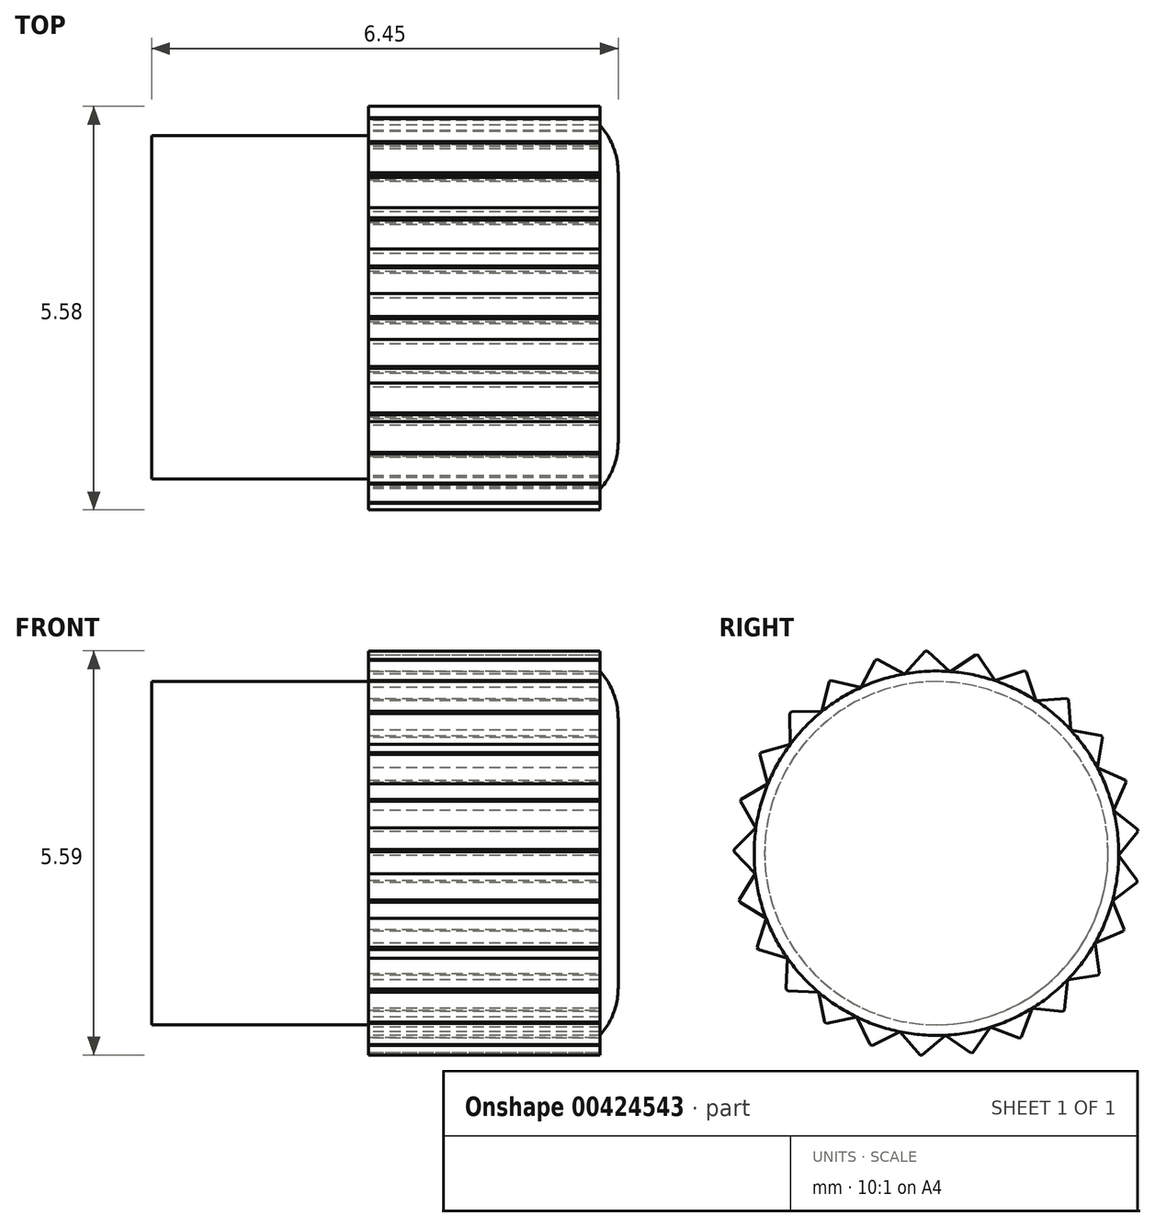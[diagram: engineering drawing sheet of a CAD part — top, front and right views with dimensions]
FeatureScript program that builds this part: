
annotation { "Feature Type Name" : "Feature", "Feature Type Description" : "" }
export const myFeature = defineFeature(function(context is Context, id is Id, definition is map)
    precondition{}
    {
        {
            var Q0;
            Q0=qCreatedBy(makeId("Right.planeOp"),FACE);
            var sketch = newSketch(context, id + "F0", { "sketchPlane" : qUnion([Q0])});
            skCircle(sketch, "E0.cCircle", {"center": v(0, 0) * mm, "radius": 2.5 * mm, "construction": true});
            skLineSegment(sketch, "E0.0", {"start": v(2.2, -1.24) * mm, "end": v(1.81, -1.75) * mm});
            skLineSegment(sketch, "E0.1", {"start": v(1.81, -1.75) * mm, "end": v(1.32, -2.14) * mm});
            skLineSegment(sketch, "E0.2", {"start": v(1.32, -2.14) * mm, "end": v(0.75, -2.4) * mm});
            skLineSegment(sketch, "E0.3", {"start": v(0.75, -2.4) * mm, "end": v(0.13, -2.52) * mm});
            skLineSegment(sketch, "E0.4", {"start": v(0.13, -2.52) * mm, "end": v(-0.5, -2.47) * mm});
            skLineSegment(sketch, "E0.5", {"start": v(-0.5, -2.47) * mm, "end": v(-1.1, -2.27) * mm});
            skLineSegment(sketch, "E0.6", {"start": v(-1.1, -2.27) * mm, "end": v(-1.63, -1.92) * mm});
            skLineSegment(sketch, "E0.7", {"start": v(-1.63, -1.92) * mm, "end": v(-2.06, -1.45) * mm});
            skLineSegment(sketch, "E0.8", {"start": v(-2.06, -1.45) * mm, "end": v(-2.35, -0.9) * mm});
            skLineSegment(sketch, "E0.9", {"start": v(-2.35, -0.9) * mm, "end": v(-2.5, -0.28) * mm});
            skLineSegment(sketch, "E0.10", {"start": v(-2.5, -0.28) * mm, "end": v(-2.5, 0.35) * mm});
            skLineSegment(sketch, "E0.11", {"start": v(-2.5, 0.35) * mm, "end": v(-2.33, 0.96) * mm});
            skLineSegment(sketch, "E0.12", {"start": v(-2.33, 0.96) * mm, "end": v(-2.02, 1.5) * mm});
            skLineSegment(sketch, "E0.13", {"start": v(-2.02, 1.5) * mm, "end": v(-1.58, 1.96) * mm});
            skLineSegment(sketch, "E0.14", {"start": v(-1.58, 1.96) * mm, "end": v(-1.04, 2.3) * mm});
            skLineSegment(sketch, "E0.15", {"start": v(-1.04, 2.3) * mm, "end": v(-0.44, 2.48) * mm});
            skLineSegment(sketch, "E0.16", {"start": v(-0.44, 2.48) * mm, "end": v(0.2, 2.51) * mm});
            skLineSegment(sketch, "E0.17", {"start": v(0.2, 2.51) * mm, "end": v(0.8, 2.39) * mm});
            skLineSegment(sketch, "E0.18", {"start": v(0.8, 2.39) * mm, "end": v(1.38, 2.1) * mm});
            skLineSegment(sketch, "E0.19", {"start": v(1.38, 2.1) * mm, "end": v(1.86, 1.7) * mm});
            skLineSegment(sketch, "E0.20", {"start": v(1.86, 1.7) * mm, "end": v(2.22, 1.19) * mm});
            skLineSegment(sketch, "E0.21", {"start": v(2.22, 1.19) * mm, "end": v(2.45, 0.6) * mm});
            skLineSegment(sketch, "E0.22", {"start": v(2.45, 0.6) * mm, "end": v(2.52, -0.03) * mm});
            skLineSegment(sketch, "E0.23", {"start": v(2.52, -0.03) * mm, "end": v(2.43, -0.66) * mm});
            skLineSegment(sketch, "E0.24", {"start": v(2.43, -0.66) * mm, "end": v(2.2, -1.24) * mm});
            skPoint(sketch, "E0.0.midPoint", {"position": v(2, -1.5) * mm});
            skSolve(sketch);
        }
        {
            var Q0;
            Q0=makeQuery(id+"F0.imprint","IMPRINT",FACE,{"disambiguationData":[TD([[makeQuery(id+"F0.imprint","IMPRINT",EDGE,{"derivedFrom":sQuery(id+"F0.wireOp",EDGE,"E0.0")}),-1.0]])]});
            extrude(context, id + "F1", {"entities" : qUnion([Q0]), "depth" : 3.2 * mm});
        }
        {
            var Q0;
            Q0=makeQuery(id+"F1.opExtrude","SWEPT_FACE",FACE,{"disambiguationData":[OSD([sQuery(id+"F0.wireOp",EDGE,"E0.14")])]});
            extrude(context, id + "F2", {"entities" : qUnion([Q0]), "operationType" : NewBodyOperationType.ADD, "depth" : .3 * mm});
        }
        {
            var Q0;
            Q0=makeQuery(id+"F2.opExtrude","CAP_EDGE",EDGE,{"disambiguationData":[OSD([sQuery(id+"F0.wireOp",EDGE,"E0.13"),sQuery(id+"F0.wireOp",EDGE,"E0.14")])],"isStart":false});
            var Q1;
            Q1=makeQuery(id+"F2.opExtrude","CAP_EDGE",EDGE,{"disambiguationData":[OSD([sQuery(id+"F0.wireOp",EDGE,"E0.14"),sQuery(id+"F0.wireOp",EDGE,"E0.15")])],"isStart":false});
            chamfer(context, id + "F3", {"entities" : qUnion([Q0, Q1]), "width" : .3 * mm, "tangentPropagation" : true});
        }
        {
            var Q0;
            Q0=makeQuery(id+"F1.opExtrude","SWEPT_FACE",FACE,{"disambiguationData":[OSD([sQuery(id+"F0.wireOp",EDGE,"E0.15")])]});
            extrude(context, id + "F4", {"entities" : qUnion([Q0]), "operationType" : NewBodyOperationType.ADD, "depth" : .3 * mm});
        }
        {
            var Q0;
            Q0=makeQuery(id+"F1.opExtrude","SWEPT_FACE",FACE,{"disambiguationData":[OSD([sQuery(id+"F0.wireOp",EDGE,"E0.17")])]});
            extrude(context, id + "F5", {"entities" : qUnion([Q0]), "operationType" : NewBodyOperationType.ADD, "depth" : .3 * mm});
        }
        {
            var Q0;
            Q0=makeQuery(id+"F1.opExtrude","SWEPT_FACE",FACE,{"disambiguationData":[OSD([sQuery(id+"F0.wireOp",EDGE,"E0.19")])]});
            extrude(context, id + "F6", {"entities" : qUnion([Q0]), "operationType" : NewBodyOperationType.ADD, "depth" : .3 * mm});
        }
        {
            var Q0;
            Q0=makeQuery(id+"F1.opExtrude","SWEPT_FACE",FACE,{"disambiguationData":[OSD([sQuery(id+"F0.wireOp",EDGE,"E0.13")])]});
            extrude(context, id + "F7", {"entities" : qUnion([Q0]), "operationType" : NewBodyOperationType.ADD, "depth" : .3 * mm});
        }
        {
            var Q0;
            Q0=makeQuery(id+"F1.opExtrude","SWEPT_FACE",FACE,{"disambiguationData":[OSD([sQuery(id+"F0.wireOp",EDGE,"E0.11")])]});
            extrude(context, id + "F8", {"entities" : qUnion([Q0]), "operationType" : NewBodyOperationType.ADD, "depth" : .3 * mm});
        }
        {
            var Q0;
            Q0=makeQuery(id+"F6.opExtrude","CAP_EDGE",EDGE,{"disambiguationData":[OSD([sQuery(id+"F0.wireOp",EDGE,"E0.18"),sQuery(id+"F0.wireOp",EDGE,"E0.19")])],"isStart":false});
            var Q1;
            Q1=makeQuery(id+"F6.opExtrude","CAP_EDGE",EDGE,{"disambiguationData":[OSD([sQuery(id+"F0.wireOp",EDGE,"E0.19"),sQuery(id+"F0.wireOp",EDGE,"E0.20")])],"isStart":false});
            var Q2;
            Q2=makeQuery(id+"F5.opExtrude","CAP_EDGE",EDGE,{"disambiguationData":[OSD([sQuery(id+"F0.wireOp",EDGE,"E0.17"),sQuery(id+"F0.wireOp",EDGE,"E0.18")])],"isStart":false});
            var Q3;
            Q3=makeQuery(id+"F5.opExtrude","CAP_EDGE",EDGE,{"disambiguationData":[OSD([sQuery(id+"F0.wireOp",EDGE,"E0.16"),sQuery(id+"F0.wireOp",EDGE,"E0.17")])],"isStart":false});
            var Q4;
            Q4=makeQuery(id+"F4.opExtrude","CAP_EDGE",EDGE,{"disambiguationData":[OSD([sQuery(id+"F0.wireOp",EDGE,"E0.15"),sQuery(id+"F0.wireOp",EDGE,"E0.16")])],"isStart":false});
            var Q5;
            Q5=makeQuery(id+"F4.opExtrude","CAP_EDGE",EDGE,{"disambiguationData":[OSD([sQuery(id+"F0.wireOp",EDGE,"E0.14"),sQuery(id+"F0.wireOp",EDGE,"E0.15")])],"isStart":false});
            var Q6;
            Q6=makeQuery(id+"F7.opExtrude","CAP_EDGE",EDGE,{"disambiguationData":[OSD([sQuery(id+"F0.wireOp",EDGE,"E0.13"),sQuery(id+"F0.wireOp",EDGE,"E0.14")])],"isStart":false});
            var Q7;
            Q7=makeQuery(id+"F7.opExtrude","CAP_EDGE",EDGE,{"disambiguationData":[OSD([sQuery(id+"F0.wireOp",EDGE,"E0.12"),sQuery(id+"F0.wireOp",EDGE,"E0.13")])],"isStart":false});
            var Q8;
            Q8=makeQuery(id+"F8.opExtrude","CAP_EDGE",EDGE,{"disambiguationData":[OSD([sQuery(id+"F0.wireOp",EDGE,"E0.11"),sQuery(id+"F0.wireOp",EDGE,"E0.12")])],"isStart":false});
            var Q9;
            Q9=makeQuery(id+"F8.opExtrude","CAP_EDGE",EDGE,{"disambiguationData":[OSD([sQuery(id+"F0.wireOp",EDGE,"E0.10"),sQuery(id+"F0.wireOp",EDGE,"E0.11")])],"isStart":false});
            chamfer(context, id + "F9", {"entities" : qUnion([Q0, Q1, Q2, Q3, Q4, Q5, Q6, Q7, Q8, Q9]), "width" : .3 * mm, "tangentPropagation" : true});
        }
        {
            var Q0;
            Q0=makeQuery(id+"F1.opExtrude","SWEPT_FACE",FACE,{"disambiguationData":[OSD([sQuery(id+"F0.wireOp",EDGE,"E0.12")])]});
            extrude(context, id + "F10", {"entities" : qUnion([Q0]), "operationType" : NewBodyOperationType.ADD, "depth" : .3 * mm});
        }
        {
            var Q0;
            Q0=makeQuery(id+"F1.opExtrude","SWEPT_FACE",FACE,{"disambiguationData":[OSD([sQuery(id+"F0.wireOp",EDGE,"E0.16")])]});
            extrude(context, id + "F11", {"entities" : qUnion([Q0]), "operationType" : NewBodyOperationType.ADD, "depth" : .3 * mm});
        }
        {
            var Q0;
            Q0=makeQuery(id+"F1.opExtrude","SWEPT_FACE",FACE,{"disambiguationData":[OSD([sQuery(id+"F0.wireOp",EDGE,"E0.18")])]});
            extrude(context, id + "F12", {"entities" : qUnion([Q0]), "operationType" : NewBodyOperationType.ADD, "depth" : .3 * mm});
        }
        {
            var Q0;
            Q0=makeQuery(id+"F1.opExtrude","SWEPT_FACE",FACE,{"disambiguationData":[OSD([sQuery(id+"F0.wireOp",EDGE,"E0.20")])]});
            extrude(context, id + "F13", {"entities" : qUnion([Q0]), "operationType" : NewBodyOperationType.ADD, "depth" : .3 * mm});
        }
        {
            var Q0;
            Q0=makeQuery(id+"F1.opExtrude","SWEPT_FACE",FACE,{"disambiguationData":[OSD([sQuery(id+"F0.wireOp",EDGE,"E0.24")])]});
            extrude(context, id + "F14", {"entities" : qUnion([Q0]), "operationType" : NewBodyOperationType.ADD, "depth" : .3 * mm});
        }
        {
            var Q0;
            Q0=makeQuery(id+"F1.opExtrude","SWEPT_FACE",FACE,{"disambiguationData":[OSD([sQuery(id+"F0.wireOp",EDGE,"E0.22")])]});
            extrude(context, id + "F15", {"entities" : qUnion([Q0]), "operationType" : NewBodyOperationType.ADD, "depth" : .3 * mm});
        }
        {
            var Q0;
            Q0=makeQuery(id+"F1.opExtrude","SWEPT_FACE",FACE,{"disambiguationData":[OSD([sQuery(id+"F0.wireOp",EDGE,"E0.1")])]});
            extrude(context, id + "F16", {"entities" : qUnion([Q0]), "operationType" : NewBodyOperationType.ADD, "depth" : .3 * mm});
        }
        {
            var Q0;
            Q0=makeQuery(id+"F1.opExtrude","SWEPT_FACE",FACE,{"disambiguationData":[OSD([sQuery(id+"F0.wireOp",EDGE,"E0.3")])]});
            extrude(context, id + "F17", {"entities" : qUnion([Q0]), "operationType" : NewBodyOperationType.ADD, "depth" : .3 * mm});
        }
        {
            var Q0;
            Q0=makeQuery(id+"F1.opExtrude","SWEPT_FACE",FACE,{"disambiguationData":[OSD([sQuery(id+"F0.wireOp",EDGE,"E0.5")])]});
            extrude(context, id + "F18", {"entities" : qUnion([Q0]), "operationType" : NewBodyOperationType.ADD, "depth" : .3 * mm});
        }
        {
            var Q0;
            Q0=makeQuery(id+"F1.opExtrude","SWEPT_FACE",FACE,{"disambiguationData":[OSD([sQuery(id+"F0.wireOp",EDGE,"E0.7")])]});
            extrude(context, id + "F19", {"entities" : qUnion([Q0]), "operationType" : NewBodyOperationType.ADD, "depth" : .3 * mm});
        }
        {
            var Q0;
            Q0=makeQuery(id+"F1.opExtrude","SWEPT_FACE",FACE,{"disambiguationData":[OSD([sQuery(id+"F0.wireOp",EDGE,"E0.9")])]});
            extrude(context, id + "F20", {"entities" : qUnion([Q0]), "operationType" : NewBodyOperationType.ADD, "depth" : .3 * mm});
        }
        {
            var Q0;
            Q0=makeQuery(id+"F20.opExtrude","CAP_EDGE",EDGE,{"disambiguationData":[OSD([sQuery(id+"F0.wireOp",EDGE,"E0.8"),sQuery(id+"F0.wireOp",EDGE,"E0.9")])],"isStart":false});
            var Q1;
            Q1=makeQuery(id+"F20.opExtrude","CAP_EDGE",EDGE,{"disambiguationData":[OSD([sQuery(id+"F0.wireOp",EDGE,"E0.9"),sQuery(id+"F0.wireOp",EDGE,"E0.10")])],"isStart":false});
            var Q2;
            Q2=makeQuery(id+"F19.opExtrude","CAP_EDGE",EDGE,{"disambiguationData":[OSD([sQuery(id+"F0.wireOp",EDGE,"E0.7"),sQuery(id+"F0.wireOp",EDGE,"E0.8")])],"isStart":false});
            var Q3;
            Q3=makeQuery(id+"F19.opExtrude","CAP_EDGE",EDGE,{"disambiguationData":[OSD([sQuery(id+"F0.wireOp",EDGE,"E0.6"),sQuery(id+"F0.wireOp",EDGE,"E0.7")])],"isStart":false});
            var Q4;
            Q4=makeQuery(id+"F18.opExtrude","CAP_EDGE",EDGE,{"disambiguationData":[OSD([sQuery(id+"F0.wireOp",EDGE,"E0.5"),sQuery(id+"F0.wireOp",EDGE,"E0.6")])],"isStart":false});
            var Q5;
            Q5=makeQuery(id+"F18.opExtrude","CAP_EDGE",EDGE,{"disambiguationData":[OSD([sQuery(id+"F0.wireOp",EDGE,"E0.4"),sQuery(id+"F0.wireOp",EDGE,"E0.5")])],"isStart":false});
            var Q6;
            Q6=makeQuery(id+"F17.opExtrude","CAP_EDGE",EDGE,{"disambiguationData":[OSD([sQuery(id+"F0.wireOp",EDGE,"E0.3"),sQuery(id+"F0.wireOp",EDGE,"E0.4")])],"isStart":false});
            var Q7;
            Q7=makeQuery(id+"F17.opExtrude","CAP_EDGE",EDGE,{"disambiguationData":[OSD([sQuery(id+"F0.wireOp",EDGE,"E0.2"),sQuery(id+"F0.wireOp",EDGE,"E0.3")])],"isStart":false});
            var Q8;
            Q8=makeQuery(id+"F16.opExtrude","CAP_EDGE",EDGE,{"disambiguationData":[OSD([sQuery(id+"F0.wireOp",EDGE,"E0.1"),sQuery(id+"F0.wireOp",EDGE,"E0.2")])],"isStart":false});
            var Q9;
            Q9=makeQuery(id+"F16.opExtrude","CAP_EDGE",EDGE,{"disambiguationData":[OSD([sQuery(id+"F0.wireOp",EDGE,"E0.0"),sQuery(id+"F0.wireOp",EDGE,"E0.1")])],"isStart":false});
            var Q10;
            Q10=makeQuery(id+"F14.opExtrude","CAP_EDGE",EDGE,{"disambiguationData":[OSD([sQuery(id+"F0.wireOp",EDGE,"E0.0"),sQuery(id+"F0.wireOp",EDGE,"E0.24")])],"isStart":false});
            var Q11;
            Q11=makeQuery(id+"F14.opExtrude","CAP_EDGE",EDGE,{"disambiguationData":[OSD([sQuery(id+"F0.wireOp",EDGE,"E0.23"),sQuery(id+"F0.wireOp",EDGE,"E0.24")])],"isStart":false});
            var Q12;
            Q12=makeQuery(id+"F15.opExtrude","CAP_EDGE",EDGE,{"disambiguationData":[OSD([sQuery(id+"F0.wireOp",EDGE,"E0.22"),sQuery(id+"F0.wireOp",EDGE,"E0.23")])],"isStart":false});
            var Q13;
            Q13=makeQuery(id+"F15.opExtrude","CAP_EDGE",EDGE,{"disambiguationData":[OSD([sQuery(id+"F0.wireOp",EDGE,"E0.21"),sQuery(id+"F0.wireOp",EDGE,"E0.22")])],"isStart":false});
            var Q14;
            Q14=makeQuery(id+"F13.opExtrude","CAP_EDGE",EDGE,{"disambiguationData":[OSD([sQuery(id+"F0.wireOp",EDGE,"E0.20"),sQuery(id+"F0.wireOp",EDGE,"E0.21")])],"isStart":false});
            var Q15;
            Q15=makeQuery(id+"F13.opExtrude","CAP_EDGE",EDGE,{"disambiguationData":[OSD([sQuery(id+"F0.wireOp",EDGE,"E0.19"),sQuery(id+"F0.wireOp",EDGE,"E0.20")])],"isStart":false});
            var Q16;
            Q16=makeQuery(id+"F12.opExtrude","CAP_EDGE",EDGE,{"disambiguationData":[OSD([sQuery(id+"F0.wireOp",EDGE,"E0.18"),sQuery(id+"F0.wireOp",EDGE,"E0.19")])],"isStart":false});
            var Q17;
            Q17=makeQuery(id+"F12.opExtrude","CAP_EDGE",EDGE,{"disambiguationData":[OSD([sQuery(id+"F0.wireOp",EDGE,"E0.17"),sQuery(id+"F0.wireOp",EDGE,"E0.18")])],"isStart":false});
            var Q18;
            Q18=makeQuery(id+"F11.opExtrude","CAP_EDGE",EDGE,{"disambiguationData":[OSD([sQuery(id+"F0.wireOp",EDGE,"E0.16"),sQuery(id+"F0.wireOp",EDGE,"E0.17")])],"isStart":false});
            var Q19;
            Q19=makeQuery(id+"F11.opExtrude","CAP_EDGE",EDGE,{"disambiguationData":[OSD([sQuery(id+"F0.wireOp",EDGE,"E0.15"),sQuery(id+"F0.wireOp",EDGE,"E0.16")])],"isStart":false});
            var Q20;
            Q20=makeQuery(id+"F10.opExtrude","CAP_EDGE",EDGE,{"disambiguationData":[OSD([sQuery(id+"F0.wireOp",EDGE,"E0.12"),sQuery(id+"F0.wireOp",EDGE,"E0.13")])],"isStart":false});
            var Q21;
            Q21=makeQuery(id+"F10.opExtrude","CAP_EDGE",EDGE,{"disambiguationData":[OSD([sQuery(id+"F0.wireOp",EDGE,"E0.11"),sQuery(id+"F0.wireOp",EDGE,"E0.12")])],"isStart":false});
            chamfer(context, id + "F21", {"entities" : qUnion([Q0, Q1, Q2, Q3, Q4, Q5, Q6, Q7, Q8, Q9, Q10, Q11, Q12, Q13, Q14, Q15, Q16, Q17, Q18, Q19, Q20, Q21]), "width" : .3 * mm, "tangentPropagation" : true});
        }
        {
            var Q0;
            Q0=makeQuery(id+"F1.opExtrude","SWEPT_FACE",FACE,{"disambiguationData":[OSD([sQuery(id+"F0.wireOp",EDGE,"E0.10")])]});
            extrude(context, id + "F22", {"entities" : qUnion([Q0]), "operationType" : NewBodyOperationType.ADD, "depth" : .3 * mm});
        }
        {
            var Q0;
            Q0=makeQuery(id+"F1.opExtrude","SWEPT_FACE",FACE,{"disambiguationData":[OSD([sQuery(id+"F0.wireOp",EDGE,"E0.8")])]});
            extrude(context, id + "F23", {"entities" : qUnion([Q0]), "operationType" : NewBodyOperationType.ADD, "depth" : .3 * mm});
        }
        {
            var Q0;
            Q0=makeQuery(id+"F1.opExtrude","SWEPT_FACE",FACE,{"disambiguationData":[OSD([sQuery(id+"F0.wireOp",EDGE,"E0.6")])]});
            extrude(context, id + "F24", {"entities" : qUnion([Q0]), "operationType" : NewBodyOperationType.ADD, "depth" : .3 * mm});
        }
        {
            var Q0;
            Q0=makeQuery(id+"F1.opExtrude","SWEPT_FACE",FACE,{"disambiguationData":[OSD([sQuery(id+"F0.wireOp",EDGE,"E0.4")])]});
            extrude(context, id + "F25", {"entities" : qUnion([Q0]), "operationType" : NewBodyOperationType.ADD, "depth" : .3 * mm});
        }
        {
            var Q0;
            Q0=makeQuery(id+"F1.opExtrude","SWEPT_FACE",FACE,{"disambiguationData":[OSD([sQuery(id+"F0.wireOp",EDGE,"E0.2")])]});
            extrude(context, id + "F26", {"entities" : qUnion([Q0]), "operationType" : NewBodyOperationType.ADD, "depth" : .3 * mm});
        }
        {
            var Q0;
            Q0=makeQuery(id+"F1.opExtrude","SWEPT_FACE",FACE,{"disambiguationData":[OSD([sQuery(id+"F0.wireOp",EDGE,"E0.0")])]});
            extrude(context, id + "F27", {"entities" : qUnion([Q0]), "operationType" : NewBodyOperationType.ADD, "depth" : .3 * mm});
        }
        {
            var Q0;
            Q0=makeQuery(id+"F1.opExtrude","SWEPT_FACE",FACE,{"disambiguationData":[OSD([sQuery(id+"F0.wireOp",EDGE,"E0.23")])]});
            extrude(context, id + "F28", {"entities" : qUnion([Q0]), "operationType" : NewBodyOperationType.ADD, "depth" : .3 * mm});
        }
        {
            var Q0;
            Q0=makeQuery(id+"F1.opExtrude","SWEPT_FACE",FACE,{"disambiguationData":[OSD([sQuery(id+"F0.wireOp",EDGE,"E0.21")])]});
            extrude(context, id + "F29", {"entities" : qUnion([Q0]), "operationType" : NewBodyOperationType.ADD, "depth" : .3 * mm});
        }
        {
            var Q0;
            Q0=makeQuery(id+"F29.opExtrude","CAP_EDGE",EDGE,{"disambiguationData":[OSD([sQuery(id+"F0.wireOp",EDGE,"E0.20"),sQuery(id+"F0.wireOp",EDGE,"E0.21")])],"isStart":false});
            var Q1;
            Q1=makeQuery(id+"F29.opExtrude","CAP_EDGE",EDGE,{"disambiguationData":[OSD([sQuery(id+"F0.wireOp",EDGE,"E0.21"),sQuery(id+"F0.wireOp",EDGE,"E0.22")])],"isStart":false});
            var Q2;
            Q2=makeQuery(id+"F28.opExtrude","CAP_EDGE",EDGE,{"disambiguationData":[OSD([sQuery(id+"F0.wireOp",EDGE,"E0.22"),sQuery(id+"F0.wireOp",EDGE,"E0.23")])],"isStart":false});
            var Q3;
            Q3=makeQuery(id+"F28.opExtrude","CAP_EDGE",EDGE,{"disambiguationData":[OSD([sQuery(id+"F0.wireOp",EDGE,"E0.23"),sQuery(id+"F0.wireOp",EDGE,"E0.24")])],"isStart":false});
            var Q4;
            Q4=makeQuery(id+"F27.opExtrude","CAP_EDGE",EDGE,{"disambiguationData":[OSD([sQuery(id+"F0.wireOp",EDGE,"E0.0"),sQuery(id+"F0.wireOp",EDGE,"E0.24")])],"isStart":false});
            var Q5;
            Q5=makeQuery(id+"F27.opExtrude","CAP_EDGE",EDGE,{"disambiguationData":[OSD([sQuery(id+"F0.wireOp",EDGE,"E0.0"),sQuery(id+"F0.wireOp",EDGE,"E0.1")])],"isStart":false});
            var Q6;
            Q6=makeQuery(id+"F26.opExtrude","CAP_EDGE",EDGE,{"disambiguationData":[OSD([sQuery(id+"F0.wireOp",EDGE,"E0.1"),sQuery(id+"F0.wireOp",EDGE,"E0.2")])],"isStart":false});
            var Q7;
            Q7=makeQuery(id+"F26.opExtrude","CAP_EDGE",EDGE,{"disambiguationData":[OSD([sQuery(id+"F0.wireOp",EDGE,"E0.2"),sQuery(id+"F0.wireOp",EDGE,"E0.3")])],"isStart":false});
            var Q8;
            Q8=makeQuery(id+"F25.opExtrude","CAP_EDGE",EDGE,{"disambiguationData":[OSD([sQuery(id+"F0.wireOp",EDGE,"E0.4"),sQuery(id+"F0.wireOp",EDGE,"E0.5")])],"isStart":false});
            var Q9;
            Q9=makeQuery(id+"F25.opExtrude","CAP_EDGE",EDGE,{"disambiguationData":[OSD([sQuery(id+"F0.wireOp",EDGE,"E0.3"),sQuery(id+"F0.wireOp",EDGE,"E0.4")])],"isStart":false});
            var Q10;
            Q10=makeQuery(id+"F24.opExtrude","CAP_EDGE",EDGE,{"disambiguationData":[OSD([sQuery(id+"F0.wireOp",EDGE,"E0.5"),sQuery(id+"F0.wireOp",EDGE,"E0.6")])],"isStart":false});
            var Q11;
            Q11=makeQuery(id+"F24.opExtrude","CAP_EDGE",EDGE,{"disambiguationData":[OSD([sQuery(id+"F0.wireOp",EDGE,"E0.6"),sQuery(id+"F0.wireOp",EDGE,"E0.7")])],"isStart":false});
            var Q12;
            Q12=makeQuery(id+"F23.opExtrude","CAP_EDGE",EDGE,{"disambiguationData":[OSD([sQuery(id+"F0.wireOp",EDGE,"E0.7"),sQuery(id+"F0.wireOp",EDGE,"E0.8")])],"isStart":false});
            var Q13;
            Q13=makeQuery(id+"F23.opExtrude","CAP_EDGE",EDGE,{"disambiguationData":[OSD([sQuery(id+"F0.wireOp",EDGE,"E0.8"),sQuery(id+"F0.wireOp",EDGE,"E0.9")])],"isStart":false});
            var Q14;
            Q14=makeQuery(id+"F22.opExtrude","CAP_EDGE",EDGE,{"disambiguationData":[OSD([sQuery(id+"F0.wireOp",EDGE,"E0.9"),sQuery(id+"F0.wireOp",EDGE,"E0.10")])],"isStart":false});
            var Q15;
            Q15=makeQuery(id+"F22.opExtrude","CAP_EDGE",EDGE,{"disambiguationData":[OSD([sQuery(id+"F0.wireOp",EDGE,"E0.10"),sQuery(id+"F0.wireOp",EDGE,"E0.11")])],"isStart":false});
            chamfer(context, id + "F30", {"entities" : qUnion([Q0, Q1, Q2, Q3, Q4, Q5, Q6, Q7, Q8, Q9, Q10, Q11, Q12, Q13, Q14, Q15]), "width" : .3 * mm, "tangentPropagation" : true});
        }
        {
            var Q0;
            {var subQ0=sQuery(id+"F0.wireOp",EDGE,"E0.21");var subQ1=sQuery(id+"F0.wireOp",EDGE,"E0.23");var subQ2=sQuery(id+"F0.wireOp",EDGE,"E0.0");var subQ3=sQuery(id+"F0.wireOp",EDGE,"E0.2");var subQ4=sQuery(id+"F0.wireOp",EDGE,"E0.4");var subQ5=sQuery(id+"F0.wireOp",EDGE,"E0.6");var subQ6=sQuery(id+"F0.wireOp",EDGE,"E0.8");var subQ7=sQuery(id+"F0.wireOp",EDGE,"E0.10");var subQ8=sQuery(id+"F0.wireOp",EDGE,"E0.9");var subQ9=sQuery(id+"F0.wireOp",EDGE,"E0.7");var subQ10=sQuery(id+"F0.wireOp",EDGE,"E0.5");var subQ11=sQuery(id+"F0.wireOp",EDGE,"E0.3");var subQ12=sQuery(id+"F0.wireOp",EDGE,"E0.1");var subQ13=sQuery(id+"F0.wireOp",EDGE,"E0.22");var subQ14=sQuery(id+"F0.wireOp",EDGE,"E0.24");var subQ15=sQuery(id+"F0.wireOp",EDGE,"E0.20");var subQ16=sQuery(id+"F0.wireOp",EDGE,"E0.18");var subQ17=sQuery(id+"F0.wireOp",EDGE,"E0.16");var subQ18=sQuery(id+"F0.wireOp",EDGE,"E0.12");var subQ19=sQuery(id+"F0.wireOp",EDGE,"E0.11");var subQ20=sQuery(id+"F0.wireOp",EDGE,"E0.13");var subQ21=sQuery(id+"F0.wireOp",EDGE,"E0.19");var subQ22=sQuery(id+"F0.wireOp",EDGE,"E0.17");var subQ23=sQuery(id+"F0.wireOp",EDGE,"E0.15");var subQ24=sQuery(id+"F0.wireOp",EDGE,"E0.14");Q0=makeQuery(id+"F29.boolean.opBoolean","MERGE",FACE,{"derivedFrom":[makeQuery(id+"F28.boolean.opBoolean","MERGE",FACE,{"derivedFrom":[makeQuery(id+"F27.boolean.opBoolean","MERGE",FACE,{"derivedFrom":[makeQuery(id+"F26.boolean.opBoolean","MERGE",FACE,{"derivedFrom":[makeQuery(id+"F25.boolean.opBoolean","MERGE",FACE,{"derivedFrom":[makeQuery(id+"F24.boolean.opBoolean","MERGE",FACE,{"derivedFrom":[makeQuery(id+"F23.boolean.opBoolean","MERGE",FACE,{"derivedFrom":[makeQuery(id+"F22.boolean.opBoolean","MERGE",FACE,{"derivedFrom":[makeQuery(id+"F20.boolean.opBoolean","MERGE",FACE,{"derivedFrom":[makeQuery(id+"F19.boolean.opBoolean","MERGE",FACE,{"derivedFrom":[makeQuery(id+"F18.boolean.opBoolean","MERGE",FACE,{"derivedFrom":[makeQuery(id+"F17.boolean.opBoolean","MERGE",FACE,{"derivedFrom":[makeQuery(id+"F16.boolean.opBoolean","MERGE",FACE,{"derivedFrom":[makeQuery(id+"F15.boolean.opBoolean","MERGE",FACE,{"derivedFrom":[makeQuery(id+"F14.boolean.opBoolean","MERGE",FACE,{"derivedFrom":[makeQuery(id+"F13.boolean.opBoolean","MERGE",FACE,{"derivedFrom":[makeQuery(id+"F12.boolean.opBoolean","MERGE",FACE,{"derivedFrom":[makeQuery(id+"F11.boolean.opBoolean","MERGE",FACE,{"derivedFrom":[makeQuery(id+"F10.boolean.opBoolean","MERGE",FACE,{"derivedFrom":[makeQuery(id+"F8.boolean.opBoolean","MERGE",FACE,{"derivedFrom":[makeQuery(id+"F7.boolean.opBoolean","MERGE",FACE,{"derivedFrom":[makeQuery(id+"F6.boolean.opBoolean","MERGE",FACE,{"derivedFrom":[makeQuery(id+"F5.boolean.opBoolean","MERGE",FACE,{"derivedFrom":[makeQuery(id+"F4.boolean.opBoolean","MERGE",FACE,{"derivedFrom":[makeQuery(id+"F2.boolean.opBoolean","MERGE",FACE,{"derivedFrom":[makeQuery(id+"F1.opExtrude","CAP_FACE",FACE,{"disambiguationData":[OSD([subQ2,subQ12,subQ3,subQ11,subQ4,subQ10,subQ5,subQ9,subQ6,subQ8,subQ7,subQ19,subQ18,subQ20,subQ24,subQ23,subQ17,subQ22,subQ16,subQ21,subQ15,subQ0,subQ13,subQ1,subQ14])],"isStart":false}),makeQuery(id+"F2.opExtrude","SWEPT_FACE",FACE,{"disambiguationData":[OSD([subQ24]),TDD([makeQuery(id+"F1.opExtrude","CAP_EDGE",EDGE,{"disambiguationData":[OSD([subQ24])],"isStart":false})])]})]}),makeQuery(id+"F4.opExtrude","SWEPT_FACE",FACE,{"disambiguationData":[OSD([subQ23]),TDD([makeQuery(id+"F1.opExtrude","CAP_EDGE",EDGE,{"disambiguationData":[OSD([subQ23])],"isStart":false})])]})]}),makeQuery(id+"F5.opExtrude","SWEPT_FACE",FACE,{"disambiguationData":[OSD([subQ22]),TDD([makeQuery(id+"F1.opExtrude","CAP_EDGE",EDGE,{"disambiguationData":[OSD([subQ22])],"isStart":false})])]})]}),makeQuery(id+"F6.opExtrude","SWEPT_FACE",FACE,{"disambiguationData":[OSD([subQ21]),TDD([makeQuery(id+"F1.opExtrude","CAP_EDGE",EDGE,{"disambiguationData":[OSD([subQ21])],"isStart":false})])]})]}),makeQuery(id+"F7.opExtrude","SWEPT_FACE",FACE,{"disambiguationData":[OSD([subQ20]),TDD([makeQuery(id+"F1.opExtrude","CAP_EDGE",EDGE,{"disambiguationData":[OSD([subQ20])],"isStart":false})])]})]}),makeQuery(id+"F8.opExtrude","SWEPT_FACE",FACE,{"disambiguationData":[OSD([subQ19]),TDD([makeQuery(id+"F1.opExtrude","CAP_EDGE",EDGE,{"disambiguationData":[OSD([subQ19])],"isStart":false})])]})]}),makeQuery(id+"F10.opExtrude","SWEPT_FACE",FACE,{"disambiguationData":[OSD([subQ18]),TDD([makeQuery(id+"F1.opExtrude","CAP_EDGE",EDGE,{"disambiguationData":[OSD([subQ18])],"isStart":false})])]})]}),makeQuery(id+"F11.opExtrude","SWEPT_FACE",FACE,{"disambiguationData":[OSD([subQ17]),TDD([makeQuery(id+"F1.opExtrude","CAP_EDGE",EDGE,{"disambiguationData":[OSD([subQ17])],"isStart":false})])]})]}),makeQuery(id+"F12.opExtrude","SWEPT_FACE",FACE,{"disambiguationData":[OSD([subQ16]),TDD([makeQuery(id+"F1.opExtrude","CAP_EDGE",EDGE,{"disambiguationData":[OSD([subQ16])],"isStart":false})])]})]}),makeQuery(id+"F13.opExtrude","SWEPT_FACE",FACE,{"disambiguationData":[OSD([subQ15]),TDD([makeQuery(id+"F1.opExtrude","CAP_EDGE",EDGE,{"disambiguationData":[OSD([subQ15])],"isStart":false})])]})]}),makeQuery(id+"F14.opExtrude","SWEPT_FACE",FACE,{"disambiguationData":[OSD([subQ14]),TDD([makeQuery(id+"F1.opExtrude","CAP_EDGE",EDGE,{"disambiguationData":[OSD([subQ14])],"isStart":false})])]})]}),makeQuery(id+"F15.opExtrude","SWEPT_FACE",FACE,{"disambiguationData":[OSD([subQ13]),TDD([makeQuery(id+"F1.opExtrude","CAP_EDGE",EDGE,{"disambiguationData":[OSD([subQ13])],"isStart":false})])]})]}),makeQuery(id+"F16.opExtrude","SWEPT_FACE",FACE,{"disambiguationData":[OSD([subQ12]),TDD([makeQuery(id+"F1.opExtrude","CAP_EDGE",EDGE,{"disambiguationData":[OSD([subQ12])],"isStart":false})])]})]}),makeQuery(id+"F17.opExtrude","SWEPT_FACE",FACE,{"disambiguationData":[OSD([subQ11]),TDD([makeQuery(id+"F1.opExtrude","CAP_EDGE",EDGE,{"disambiguationData":[OSD([subQ11])],"isStart":false})])]})]}),makeQuery(id+"F18.opExtrude","SWEPT_FACE",FACE,{"disambiguationData":[OSD([subQ10]),TDD([makeQuery(id+"F1.opExtrude","CAP_EDGE",EDGE,{"disambiguationData":[OSD([subQ10])],"isStart":false})])]})]}),makeQuery(id+"F19.opExtrude","SWEPT_FACE",FACE,{"disambiguationData":[OSD([subQ9]),TDD([makeQuery(id+"F1.opExtrude","CAP_EDGE",EDGE,{"disambiguationData":[OSD([subQ9])],"isStart":false})])]})]}),makeQuery(id+"F20.opExtrude","SWEPT_FACE",FACE,{"disambiguationData":[OSD([subQ8]),TDD([makeQuery(id+"F1.opExtrude","CAP_EDGE",EDGE,{"disambiguationData":[OSD([subQ8])],"isStart":false})])]})]}),makeQuery(id+"F22.opExtrude","SWEPT_FACE",FACE,{"disambiguationData":[OSD([subQ7]),TDD([makeQuery(id+"F1.opExtrude","CAP_EDGE",EDGE,{"disambiguationData":[OSD([subQ7])],"isStart":false})])]})]}),makeQuery(id+"F23.opExtrude","SWEPT_FACE",FACE,{"disambiguationData":[OSD([subQ6]),TDD([makeQuery(id+"F1.opExtrude","CAP_EDGE",EDGE,{"disambiguationData":[OSD([subQ6])],"isStart":false})])]})]}),makeQuery(id+"F24.opExtrude","SWEPT_FACE",FACE,{"disambiguationData":[OSD([subQ5]),TDD([makeQuery(id+"F1.opExtrude","CAP_EDGE",EDGE,{"disambiguationData":[OSD([subQ5])],"isStart":false})])]})]}),makeQuery(id+"F25.opExtrude","SWEPT_FACE",FACE,{"disambiguationData":[OSD([subQ4]),TDD([makeQuery(id+"F1.opExtrude","CAP_EDGE",EDGE,{"disambiguationData":[OSD([subQ4])],"isStart":false})])]})]}),makeQuery(id+"F26.opExtrude","SWEPT_FACE",FACE,{"disambiguationData":[OSD([subQ3]),TDD([makeQuery(id+"F1.opExtrude","CAP_EDGE",EDGE,{"disambiguationData":[OSD([subQ3])],"isStart":false})])]})]}),makeQuery(id+"F27.opExtrude","SWEPT_FACE",FACE,{"disambiguationData":[OSD([subQ2]),TDD([makeQuery(id+"F1.opExtrude","CAP_EDGE",EDGE,{"disambiguationData":[OSD([subQ2])],"isStart":false})])]})]}),makeQuery(id+"F28.opExtrude","SWEPT_FACE",FACE,{"disambiguationData":[OSD([subQ1]),TDD([makeQuery(id+"F1.opExtrude","CAP_EDGE",EDGE,{"disambiguationData":[OSD([subQ1])],"isStart":false})])]})]}),makeQuery(id+"F29.opExtrude","SWEPT_FACE",FACE,{"disambiguationData":[OSD([subQ0]),TDD([makeQuery(id+"F1.opExtrude","CAP_EDGE",EDGE,{"disambiguationData":[OSD([subQ0])],"isStart":false})])]})]});}
            var sketch = newSketch(context, id + "F31", { "sketchPlane" : qUnion([Q0])});
            skCircle(sketch, "E1", {"center": v(0, 0) * mm, "radius": 2.52 * mm});
            skSolve(sketch);
        }
        {
            var Q0;
            {var subQ0=sQuery(id+"F31.wireOp",EDGE,"E1");var subQ1=sQuery(id+"F0.wireOp",EDGE,"E0.21");var subQ2=sQuery(id+"F0.wireOp",EDGE,"E0.23");var subQ3=sQuery(id+"F0.wireOp",EDGE,"E0.0");var subQ4=sQuery(id+"F0.wireOp",EDGE,"E0.2");var subQ5=sQuery(id+"F0.wireOp",EDGE,"E0.4");var subQ6=sQuery(id+"F0.wireOp",EDGE,"E0.6");var subQ7=sQuery(id+"F0.wireOp",EDGE,"E0.8");var subQ8=sQuery(id+"F0.wireOp",EDGE,"E0.10");var subQ9=sQuery(id+"F0.wireOp",EDGE,"E0.9");var subQ10=sQuery(id+"F0.wireOp",EDGE,"E0.7");var subQ11=sQuery(id+"F0.wireOp",EDGE,"E0.5");var subQ12=sQuery(id+"F0.wireOp",EDGE,"E0.3");var subQ13=sQuery(id+"F0.wireOp",EDGE,"E0.1");var subQ14=sQuery(id+"F0.wireOp",EDGE,"E0.22");var subQ15=sQuery(id+"F0.wireOp",EDGE,"E0.24");var subQ16=sQuery(id+"F0.wireOp",EDGE,"E0.20");var subQ17=sQuery(id+"F0.wireOp",EDGE,"E0.18");var subQ18=sQuery(id+"F0.wireOp",EDGE,"E0.16");var subQ19=sQuery(id+"F0.wireOp",EDGE,"E0.12");var subQ20=sQuery(id+"F0.wireOp",EDGE,"E0.11");var subQ21=sQuery(id+"F0.wireOp",EDGE,"E0.13");var subQ22=sQuery(id+"F0.wireOp",EDGE,"E0.19");var subQ23=sQuery(id+"F0.wireOp",EDGE,"E0.17");var subQ24=sQuery(id+"F0.wireOp",EDGE,"E0.15");var subQ25=sQuery(id+"F0.wireOp",EDGE,"E0.14");var subQ26=makeQuery(id+"F2.boolean.opBoolean","MERGE",FACE,{"derivedFrom":[makeQuery(id+"F1.opExtrude","CAP_FACE",FACE,{"disambiguationData":[OSD([subQ3,subQ13,subQ4,subQ12,subQ5,subQ11,subQ6,subQ10,subQ7,subQ9,subQ8,subQ20,subQ19,subQ21,subQ25,subQ24,subQ18,subQ23,subQ17,subQ22,subQ16,subQ1,subQ14,subQ2,subQ15])],"isStart":false}),makeQuery(id+"F2.opExtrude","SWEPT_FACE",FACE,{"disambiguationData":[OSD([subQ25]),TDD([makeQuery(id+"F1.opExtrude","CAP_EDGE",EDGE,{"disambiguationData":[OSD([subQ25])],"isStart":false})])]})]});var subQ27=makeQuery(id+"F8.boolean.opBoolean","MERGE",FACE,{"derivedFrom":[makeQuery(id+"F7.boolean.opBoolean","MERGE",FACE,{"derivedFrom":[makeQuery(id+"F6.boolean.opBoolean","MERGE",FACE,{"derivedFrom":[makeQuery(id+"F5.boolean.opBoolean","MERGE",FACE,{"derivedFrom":[makeQuery(id+"F4.boolean.opBoolean","MERGE",FACE,{"derivedFrom":[subQ26,makeQuery(id+"F4.opExtrude","SWEPT_FACE",FACE,{"disambiguationData":[OSD([subQ24]),TDD([makeQuery(id+"F1.opExtrude","CAP_EDGE",EDGE,{"disambiguationData":[OSD([subQ24])],"isStart":false})])]})]}),makeQuery(id+"F5.opExtrude","SWEPT_FACE",FACE,{"disambiguationData":[OSD([subQ23]),TDD([makeQuery(id+"F1.opExtrude","CAP_EDGE",EDGE,{"disambiguationData":[OSD([subQ23])],"isStart":false})])]})]}),makeQuery(id+"F6.opExtrude","SWEPT_FACE",FACE,{"disambiguationData":[OSD([subQ22]),TDD([makeQuery(id+"F1.opExtrude","CAP_EDGE",EDGE,{"disambiguationData":[OSD([subQ22])],"isStart":false})])]})]}),makeQuery(id+"F7.opExtrude","SWEPT_FACE",FACE,{"disambiguationData":[OSD([subQ21]),TDD([makeQuery(id+"F1.opExtrude","CAP_EDGE",EDGE,{"disambiguationData":[OSD([subQ21])],"isStart":false})])]})]}),makeQuery(id+"F8.opExtrude","SWEPT_FACE",FACE,{"disambiguationData":[OSD([subQ20]),TDD([makeQuery(id+"F1.opExtrude","CAP_EDGE",EDGE,{"disambiguationData":[OSD([subQ20])],"isStart":false})])]})]});var subQ51=makeQuery(id+"F31.imprint","INTERSECT",VERTEX,{"derivedFrom":[makeQuery(id+"F3.opChamfer","BLEND_EDGE",EDGE,{"blendedFrom":[makeQuery(id+"F2.opExtrude","CAP_EDGE",EDGE,{"disambiguationData":[OSD([subQ21,subQ25])],"isStart":false}),subQ26],"blendedInto":[subQ26]}),makeQuery(id+"F9.opChamfer","BLEND_EDGE",EDGE,{"blendedFrom":[makeQuery(id+"F7.opExtrude","CAP_EDGE",EDGE,{"disambiguationData":[OSD([subQ21,subQ25])],"isStart":false}),subQ27],"blendedInto":[subQ27]}),subQ0]});Q0=makeQuery(id+"F31.imprint","IMPRINT",FACE,{"disambiguationData":[TD([[makeQuery(id+"F31.imprint","IMPRINT",EDGE,{"disambiguationData":[TD([[subQ51,1.0]])],"derivedFrom":subQ0}),1.0]])]});}
            extrude(context, id + "F32", {"entities" : qUnion([Q0]), "operationType" : NewBodyOperationType.ADD, "depth" : .25 * mm});
        }
        {
            var Q0;
            Q0=makeQuery(id+"F32.opExtrude","CAP_EDGE",EDGE,{"disambiguationData":[OSD([sQuery(id+"F31.wireOp",EDGE,"E1")])],"isStart":false});
            fillet(context, id + "F33", {"entities" : qUnion([Q0]), "radius" : 1 * mm, "tangentPropagation" : true, "allowEdgeOverflow" : false});
        }
        {
            var Q0;
            {var subQ0=sQuery(id+"F0.wireOp",EDGE,"E0.21");var subQ1=sQuery(id+"F0.wireOp",EDGE,"E0.23");var subQ2=sQuery(id+"F0.wireOp",EDGE,"E0.0");var subQ3=sQuery(id+"F0.wireOp",EDGE,"E0.2");var subQ4=sQuery(id+"F0.wireOp",EDGE,"E0.4");var subQ5=sQuery(id+"F0.wireOp",EDGE,"E0.6");var subQ6=sQuery(id+"F0.wireOp",EDGE,"E0.8");var subQ7=sQuery(id+"F0.wireOp",EDGE,"E0.10");var subQ8=sQuery(id+"F0.wireOp",EDGE,"E0.9");var subQ9=sQuery(id+"F0.wireOp",EDGE,"E0.7");var subQ10=sQuery(id+"F0.wireOp",EDGE,"E0.5");var subQ11=sQuery(id+"F0.wireOp",EDGE,"E0.3");var subQ12=sQuery(id+"F0.wireOp",EDGE,"E0.1");var subQ13=sQuery(id+"F0.wireOp",EDGE,"E0.22");var subQ14=sQuery(id+"F0.wireOp",EDGE,"E0.24");var subQ15=sQuery(id+"F0.wireOp",EDGE,"E0.20");var subQ16=sQuery(id+"F0.wireOp",EDGE,"E0.18");var subQ17=sQuery(id+"F0.wireOp",EDGE,"E0.16");var subQ18=sQuery(id+"F0.wireOp",EDGE,"E0.12");var subQ19=sQuery(id+"F0.wireOp",EDGE,"E0.11");var subQ20=sQuery(id+"F0.wireOp",EDGE,"E0.13");var subQ21=sQuery(id+"F0.wireOp",EDGE,"E0.19");var subQ22=sQuery(id+"F0.wireOp",EDGE,"E0.17");var subQ23=sQuery(id+"F0.wireOp",EDGE,"E0.15");var subQ24=sQuery(id+"F0.wireOp",EDGE,"E0.14");Q0=makeQuery(id+"F29.boolean.opBoolean","MERGE",FACE,{"derivedFrom":[makeQuery(id+"F28.boolean.opBoolean","MERGE",FACE,{"derivedFrom":[makeQuery(id+"F27.boolean.opBoolean","MERGE",FACE,{"derivedFrom":[makeQuery(id+"F26.boolean.opBoolean","MERGE",FACE,{"derivedFrom":[makeQuery(id+"F25.boolean.opBoolean","MERGE",FACE,{"derivedFrom":[makeQuery(id+"F24.boolean.opBoolean","MERGE",FACE,{"derivedFrom":[makeQuery(id+"F23.boolean.opBoolean","MERGE",FACE,{"derivedFrom":[makeQuery(id+"F22.boolean.opBoolean","MERGE",FACE,{"derivedFrom":[makeQuery(id+"F20.boolean.opBoolean","MERGE",FACE,{"derivedFrom":[makeQuery(id+"F19.boolean.opBoolean","MERGE",FACE,{"derivedFrom":[makeQuery(id+"F18.boolean.opBoolean","MERGE",FACE,{"derivedFrom":[makeQuery(id+"F17.boolean.opBoolean","MERGE",FACE,{"derivedFrom":[makeQuery(id+"F16.boolean.opBoolean","MERGE",FACE,{"derivedFrom":[makeQuery(id+"F15.boolean.opBoolean","MERGE",FACE,{"derivedFrom":[makeQuery(id+"F14.boolean.opBoolean","MERGE",FACE,{"derivedFrom":[makeQuery(id+"F13.boolean.opBoolean","MERGE",FACE,{"derivedFrom":[makeQuery(id+"F12.boolean.opBoolean","MERGE",FACE,{"derivedFrom":[makeQuery(id+"F11.boolean.opBoolean","MERGE",FACE,{"derivedFrom":[makeQuery(id+"F10.boolean.opBoolean","MERGE",FACE,{"derivedFrom":[makeQuery(id+"F8.boolean.opBoolean","MERGE",FACE,{"derivedFrom":[makeQuery(id+"F7.boolean.opBoolean","MERGE",FACE,{"derivedFrom":[makeQuery(id+"F6.boolean.opBoolean","MERGE",FACE,{"derivedFrom":[makeQuery(id+"F5.boolean.opBoolean","MERGE",FACE,{"derivedFrom":[makeQuery(id+"F4.boolean.opBoolean","MERGE",FACE,{"derivedFrom":[makeQuery(id+"F2.boolean.opBoolean","MERGE",FACE,{"derivedFrom":[makeQuery(id+"F1.opExtrude","CAP_FACE",FACE,{"disambiguationData":[OSD([subQ2,subQ12,subQ3,subQ11,subQ4,subQ10,subQ5,subQ9,subQ6,subQ8,subQ7,subQ19,subQ18,subQ20,subQ24,subQ23,subQ17,subQ22,subQ16,subQ21,subQ15,subQ0,subQ13,subQ1,subQ14])],"isStart":true}),makeQuery(id+"F2.opExtrude","SWEPT_FACE",FACE,{"disambiguationData":[OSD([subQ24]),TDD([makeQuery(id+"F1.opExtrude","CAP_EDGE",EDGE,{"disambiguationData":[OSD([subQ24])],"isStart":true})])]})]}),makeQuery(id+"F4.opExtrude","SWEPT_FACE",FACE,{"disambiguationData":[OSD([subQ23]),TDD([makeQuery(id+"F1.opExtrude","CAP_EDGE",EDGE,{"disambiguationData":[OSD([subQ23])],"isStart":true})])]})]}),makeQuery(id+"F5.opExtrude","SWEPT_FACE",FACE,{"disambiguationData":[OSD([subQ22]),TDD([makeQuery(id+"F1.opExtrude","CAP_EDGE",EDGE,{"disambiguationData":[OSD([subQ22])],"isStart":true})])]})]}),makeQuery(id+"F6.opExtrude","SWEPT_FACE",FACE,{"disambiguationData":[OSD([subQ21]),TDD([makeQuery(id+"F1.opExtrude","CAP_EDGE",EDGE,{"disambiguationData":[OSD([subQ21])],"isStart":true})])]})]}),makeQuery(id+"F7.opExtrude","SWEPT_FACE",FACE,{"disambiguationData":[OSD([subQ20]),TDD([makeQuery(id+"F1.opExtrude","CAP_EDGE",EDGE,{"disambiguationData":[OSD([subQ20])],"isStart":true})])]})]}),makeQuery(id+"F8.opExtrude","SWEPT_FACE",FACE,{"disambiguationData":[OSD([subQ19]),TDD([makeQuery(id+"F1.opExtrude","CAP_EDGE",EDGE,{"disambiguationData":[OSD([subQ19])],"isStart":true})])]})]}),makeQuery(id+"F10.opExtrude","SWEPT_FACE",FACE,{"disambiguationData":[OSD([subQ18]),TDD([makeQuery(id+"F1.opExtrude","CAP_EDGE",EDGE,{"disambiguationData":[OSD([subQ18])],"isStart":true})])]})]}),makeQuery(id+"F11.opExtrude","SWEPT_FACE",FACE,{"disambiguationData":[OSD([subQ17]),TDD([makeQuery(id+"F1.opExtrude","CAP_EDGE",EDGE,{"disambiguationData":[OSD([subQ17])],"isStart":true})])]})]}),makeQuery(id+"F12.opExtrude","SWEPT_FACE",FACE,{"disambiguationData":[OSD([subQ16]),TDD([makeQuery(id+"F1.opExtrude","CAP_EDGE",EDGE,{"disambiguationData":[OSD([subQ16])],"isStart":true})])]})]}),makeQuery(id+"F13.opExtrude","SWEPT_FACE",FACE,{"disambiguationData":[OSD([subQ15]),TDD([makeQuery(id+"F1.opExtrude","CAP_EDGE",EDGE,{"disambiguationData":[OSD([subQ15])],"isStart":true})])]})]}),makeQuery(id+"F14.opExtrude","SWEPT_FACE",FACE,{"disambiguationData":[OSD([subQ14]),TDD([makeQuery(id+"F1.opExtrude","CAP_EDGE",EDGE,{"disambiguationData":[OSD([subQ14])],"isStart":true})])]})]}),makeQuery(id+"F15.opExtrude","SWEPT_FACE",FACE,{"disambiguationData":[OSD([subQ13]),TDD([makeQuery(id+"F1.opExtrude","CAP_EDGE",EDGE,{"disambiguationData":[OSD([subQ13])],"isStart":true})])]})]}),makeQuery(id+"F16.opExtrude","SWEPT_FACE",FACE,{"disambiguationData":[OSD([subQ12]),TDD([makeQuery(id+"F1.opExtrude","CAP_EDGE",EDGE,{"disambiguationData":[OSD([subQ12])],"isStart":true})])]})]}),makeQuery(id+"F17.opExtrude","SWEPT_FACE",FACE,{"disambiguationData":[OSD([subQ11]),TDD([makeQuery(id+"F1.opExtrude","CAP_EDGE",EDGE,{"disambiguationData":[OSD([subQ11])],"isStart":true})])]})]}),makeQuery(id+"F18.opExtrude","SWEPT_FACE",FACE,{"disambiguationData":[OSD([subQ10]),TDD([makeQuery(id+"F1.opExtrude","CAP_EDGE",EDGE,{"disambiguationData":[OSD([subQ10])],"isStart":true})])]})]}),makeQuery(id+"F19.opExtrude","SWEPT_FACE",FACE,{"disambiguationData":[OSD([subQ9]),TDD([makeQuery(id+"F1.opExtrude","CAP_EDGE",EDGE,{"disambiguationData":[OSD([subQ9])],"isStart":true})])]})]}),makeQuery(id+"F20.opExtrude","SWEPT_FACE",FACE,{"disambiguationData":[OSD([subQ8]),TDD([makeQuery(id+"F1.opExtrude","CAP_EDGE",EDGE,{"disambiguationData":[OSD([subQ8])],"isStart":true})])]})]}),makeQuery(id+"F22.opExtrude","SWEPT_FACE",FACE,{"disambiguationData":[OSD([subQ7]),TDD([makeQuery(id+"F1.opExtrude","CAP_EDGE",EDGE,{"disambiguationData":[OSD([subQ7])],"isStart":true})])]})]}),makeQuery(id+"F23.opExtrude","SWEPT_FACE",FACE,{"disambiguationData":[OSD([subQ6]),TDD([makeQuery(id+"F1.opExtrude","CAP_EDGE",EDGE,{"disambiguationData":[OSD([subQ6])],"isStart":true})])]})]}),makeQuery(id+"F24.opExtrude","SWEPT_FACE",FACE,{"disambiguationData":[OSD([subQ5]),TDD([makeQuery(id+"F1.opExtrude","CAP_EDGE",EDGE,{"disambiguationData":[OSD([subQ5])],"isStart":true})])]})]}),makeQuery(id+"F25.opExtrude","SWEPT_FACE",FACE,{"disambiguationData":[OSD([subQ4]),TDD([makeQuery(id+"F1.opExtrude","CAP_EDGE",EDGE,{"disambiguationData":[OSD([subQ4])],"isStart":true})])]})]}),makeQuery(id+"F26.opExtrude","SWEPT_FACE",FACE,{"disambiguationData":[OSD([subQ3]),TDD([makeQuery(id+"F1.opExtrude","CAP_EDGE",EDGE,{"disambiguationData":[OSD([subQ3])],"isStart":true})])]})]}),makeQuery(id+"F27.opExtrude","SWEPT_FACE",FACE,{"disambiguationData":[OSD([subQ2]),TDD([makeQuery(id+"F1.opExtrude","CAP_EDGE",EDGE,{"disambiguationData":[OSD([subQ2])],"isStart":true})])]})]}),makeQuery(id+"F28.opExtrude","SWEPT_FACE",FACE,{"disambiguationData":[OSD([subQ1]),TDD([makeQuery(id+"F1.opExtrude","CAP_EDGE",EDGE,{"disambiguationData":[OSD([subQ1])],"isStart":true})])]})]}),makeQuery(id+"F29.opExtrude","SWEPT_FACE",FACE,{"disambiguationData":[OSD([subQ0]),TDD([makeQuery(id+"F1.opExtrude","CAP_EDGE",EDGE,{"disambiguationData":[OSD([subQ0])],"isStart":true})])]})]});}
            var sketch = newSketch(context, id + "F34", { "sketchPlane" : qUnion([Q0])});
            skCircle(sketch, "E2", {"center": v(0, 0) * mm, "radius": 2.38 * mm});
            skSolve(sketch);
        }
        {
            var Q0;
            Q0=makeQuery(id+"F34.imprint","IMPRINT",FACE,{"disambiguationData":[TD([[makeQuery(id+"F34.imprint","IMPRINT",EDGE,{"derivedFrom":sQuery(id+"F34.wireOp",EDGE,"E2")}),1.0]])]});
            extrude(context, id + "F35", {"entities" : qUnion([Q0]), "operationType" : NewBodyOperationType.ADD, "depth" : 3 * mm});
        }
    });
